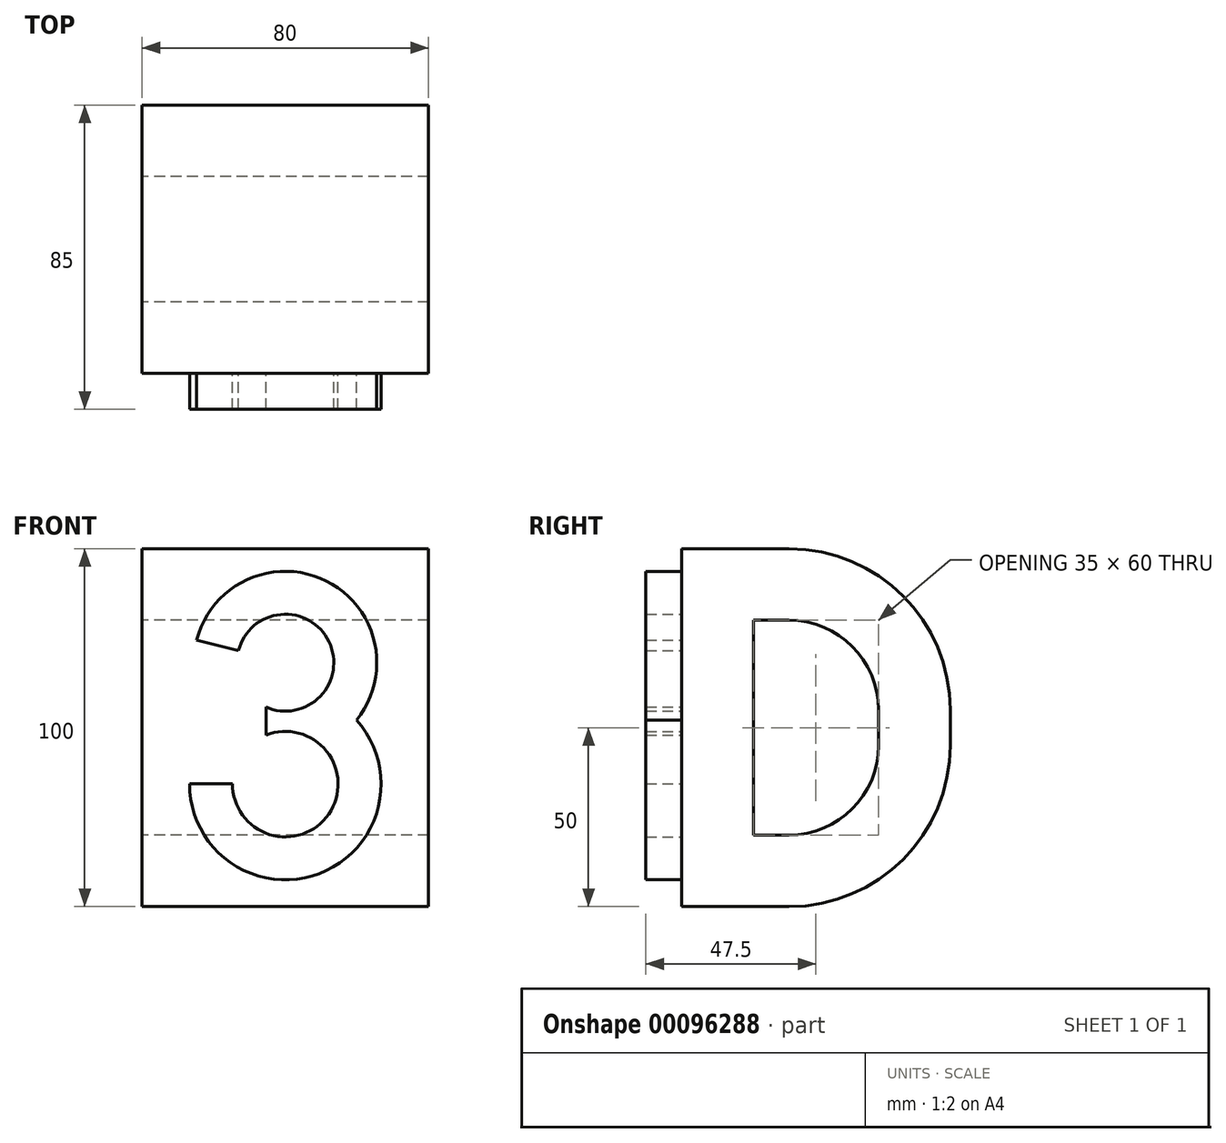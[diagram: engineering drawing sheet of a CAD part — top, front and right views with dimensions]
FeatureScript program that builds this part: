
annotation { "Feature Type Name" : "Feature", "Feature Type Description" : "" }
export const myFeature = defineFeature(function(context is Context, id is Id, definition is map)
    precondition{}
    {
        {
            var Q0;
            Q0=qCreatedBy(makeId("Right.planeOp"),FACE);
            var sketch = newSketch(context, id + "F0", { "sketchPlane" : qUnion([Q0])});
            skLineSegment(sketch, "E0.bottom", {"start": v(0, 0) * mm, "end": v(75, 0) * mm});
            skLineSegment(sketch, "E0.top", {"start": v(0, 100) * mm, "end": v(75, 100) * mm});
            skLineSegment(sketch, "E0.left", {"start": v(0, 0) * mm, "end": v(0, 100) * mm});
            skLineSegment(sketch, "E0.right", {"start": v(75, 0) * mm, "end": v(75, 100) * mm});
            skLineSegment(sketch, "E1.0", {"start": v(20, 80) * mm, "end": v(55, 80) * mm});
            skLineSegment(sketch, "E1.1", {"start": v(20, 20) * mm, "end": v(20, 80) * mm});
            skLineSegment(sketch, "E1.2", {"start": v(20, 20) * mm, "end": v(55, 20) * mm});
            skLineSegment(sketch, "E1.3", {"start": v(55, 20) * mm, "end": v(55, 80) * mm});
            skSolve(sketch);
        }
        {
            var Q0;
            Q0=qSketchRegion(id+"F0",true);
            extrude(context, id + "F1", {"entities" : qUnion([Q0]), "endBound" : BoundingType.SYMMETRIC, "depth" : 80 * mm});
        }
        {
            var Q0;
            Q0=makeQuery(id+"F1.opExtrude","SWEPT_EDGE",EDGE,{"disambiguationData":[OSD([sQuery(id+"F0.wireOp",EDGE,"E1.0"),sQuery(id+"F0.wireOp",EDGE,"E1.3")])]});
            var Q1;
            Q1=makeQuery(id+"F1.opExtrude","SWEPT_EDGE",EDGE,{"disambiguationData":[OSD([sQuery(id+"F0.wireOp",EDGE,"E1.2"),sQuery(id+"F0.wireOp",EDGE,"E1.3")])]});
            fillet(context, id + "F2", {"entities" : qUnion([Q0, Q1]), "radius" : 25 * mm, "tangentPropagation" : true, "allowEdgeOverflow" : false});
        }
        {
            var Q0;
            Q0=makeQuery(id+"F1.opExtrude","SWEPT_EDGE",EDGE,{"disambiguationData":[OSD([sQuery(id+"F0.wireOp",EDGE,"E0.top"),sQuery(id+"F0.wireOp",EDGE,"E0.right")])]});
            var Q1;
            Q1=makeQuery(id+"F1.opExtrude","SWEPT_EDGE",EDGE,{"disambiguationData":[OSD([sQuery(id+"F0.wireOp",EDGE,"E0.bottom"),sQuery(id+"F0.wireOp",EDGE,"E0.right")])]});
            fillet(context, id + "F3", {"entities" : qUnion([Q0, Q1]), "radius" : 45 * mm, "tangentPropagation" : true, "allowEdgeOverflow" : false});
        }
        {
            var Q0;
            Q0=makeQuery(id+"F1.opExtrude","SWEPT_FACE",FACE,{"disambiguationData":[OSD([sQuery(id+"F0.wireOp",EDGE,"E0.left")])]});
            var sketch = newSketch(context, id + "F4", { "sketchPlane" : qUnion([Q0])});
            skArc(sketch, "E2", {"start": v(19.88, 52.12) * mm, "mid": v(11.45, 90.99) * mm, "end": v(-24.75, 74.48) * mm});
            skArc(sketch, "E3", {"start": v(-26.74, 34.4) * mm, "mid": v(9.5, 9.23) * mm, "end": v(19.88, 52.12) * mm});
            skArc(sketch, "E4.0", {"start": v(-5.43, 55.75) * mm, "mid": v(12.2, 74.05) * mm, "end": v(-13.1, 71.61) * mm});
            skArc(sketch, "E5.0", {"start": v(-14.74, 34.4) * mm, "mid": v(12.15, 25.87) * mm, "end": v(-5.43, 47.94) * mm});
            skLineSegment(sketch, "E6", {"start": v(-13.1, 71.61) * mm, "end": v(-24.75, 74.48) * mm});
            skLineSegment(sketch, "E7", {"start": v(-14.74, 34.4) * mm, "end": v(-26.74, 34.4) * mm});
            skLineSegment(sketch, "E8", {"start": v(-5.43, 55.75) * mm, "end": v(-5.43, 47.94) * mm});
            skSolve(sketch);
        }
        {
            var Q0;
            Q0=qSketchRegion(id+"F4",true);
            extrude(context, id + "F5", {"entities" : qUnion([Q0]), "operationType" : NewBodyOperationType.ADD, "depth" : 10 * mm});
        }
    });
